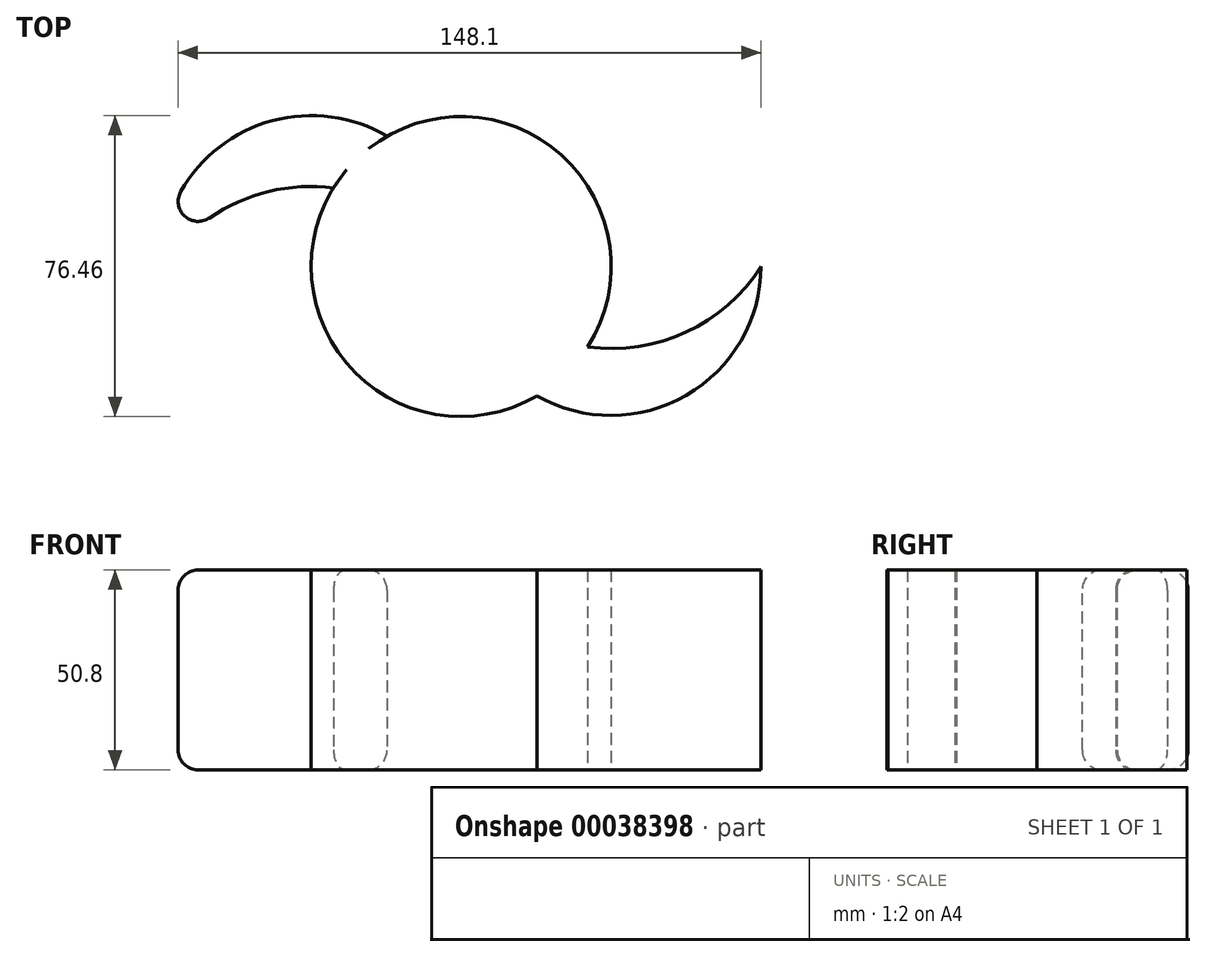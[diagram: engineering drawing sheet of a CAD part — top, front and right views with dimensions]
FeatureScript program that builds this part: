
annotation { "Feature Type Name" : "Feature", "Feature Type Description" : "" }
export const myFeature = defineFeature(function(context is Context, id is Id, definition is map)
    precondition{}
    {
        {
            var Q0;
            Q0=qCreatedBy(makeId("Top.planeOp"),FACE);
            var sketch = newSketch(context, id + "F0", { "sketchPlane" : qUnion([Q0])});
            skPoint(sketch, "E0", {"position": v(0, 0) * mm});
            skPoint(sketch, "E1", {"position": v(76.2, 0) * mm});
            skPoint(sketch, "E2", {"position": v(-76.2, 0) * mm});
            skArc(sketch, "E3", {"start": v(-18.83, 33.13) * mm, "mid": v(-57.15, 33.26) * mm, "end": v(-76.2, 0) * mm});
            skArc(sketch, "E4", {"start": v(19.27, -32.87) * mm, "mid": v(57.15, -32.74) * mm, "end": v(76.2, 0) * mm});
            skArc(sketch, "E5", {"start": v(-32.43, 20) * mm, "mid": v(-27.24, -26.64) * mm, "end": v(19.27, -32.87) * mm});
            skArc(sketch, "E6", {"start": v(-32.43, 20) * mm, "mid": v(-57.15, 16.2) * mm, "end": v(-76.2, 0) * mm});
            skArc(sketch, "E7", {"start": v(32.15, -20.45) * mm, "mid": v(57.15, -16.64) * mm, "end": v(76.2, 0) * mm});
            skArc(sketch, "E8.trimOffspring", {"start": v(32.15, -20.45) * mm, "mid": v(27.6, 26.26) * mm, "end": v(-18.83, 33.13) * mm});
            skSolve(sketch);
        }
        {
            var Q0;
            Q0 = qSketchRegion(id + "F0", true);
            extrude(context, id + "F1", {"entities" : qUnion([Q0]), "depth" : 50.8 * mm});
        }
        {
            var Q0;
            Q0=makeQuery(id+"F1.opExtrude","CAP_EDGE",EDGE,{"disambiguationData":[OSD([sQuery(id+"F0.wireOp",EDGE,"E3")])],"isStart":false});
            var Q1;
            Q1=makeQuery(id+"F1.opExtrude","CAP_EDGE",EDGE,{"disambiguationData":[OSD([sQuery(id+"F0.wireOp",EDGE,"E3")])],"isStart":true});
            var Q2;
            Q2=makeQuery(id+"F1.opExtrude","CAP_EDGE",EDGE,{"disambiguationData":[OSD([sQuery(id+"F0.wireOp",EDGE,"E6")])],"isStart":false});
            var Q3;
            Q3=makeQuery(id+"F1.opExtrude","CAP_EDGE",EDGE,{"disambiguationData":[OSD([sQuery(id+"F0.wireOp",EDGE,"E6")])],"isStart":true});
            fillet(context, id + "F2", {"entities" : qUnion([Q0, Q1, Q2, Q3]), "radius" : 5.08 * mm, "tangentPropagation" : true, "allowEdgeOverflow" : false});
        }
        {
            var Q0;
            Q0=makeQuery(id+"F1.opExtrude","SWEPT_EDGE",EDGE,{"disambiguationData":[OSD([sQuery(id+"F0.wireOp",EDGE,"E3"),sQuery(id+"F0.wireOp",EDGE,"E6")])]});
            var Q1;
            {var subQ0=sQuery(id+"F0.wireOp",EDGE,"E3");Q1=makeQuery(id+"F2.opFillet","BLEND_EDGE",EDGE,{"blendedFrom":[makeQuery(id+"F1.opExtrude","CAP_EDGE",EDGE,{"disambiguationData":[OSD([subQ0])],"isStart":true}),makeQuery(id+"F1.opExtrude","SWEPT_FACE",FACE,{"disambiguationData":[OSD([subQ0])]})],"blendedInto":[makeQuery(id+"F1.opExtrude","SWEPT_FACE",FACE,{"disambiguationData":[OSD([subQ0])]})]});}
            var Q2;
            {var subQ0=sQuery(id+"F0.wireOp",EDGE,"E6");Q2=makeQuery(id+"F2.opFillet","BLEND_EDGE",EDGE,{"blendedFrom":[makeQuery(id+"F1.opExtrude","CAP_EDGE",EDGE,{"disambiguationData":[OSD([subQ0])],"isStart":true}),makeQuery(id+"F1.opExtrude","CAP_FACE",FACE,{"disambiguationData":[OSD([sQuery(id+"F0.wireOp",EDGE,"E3"),sQuery(id+"F0.wireOp",EDGE,"E4"),sQuery(id+"F0.wireOp",EDGE,"E5"),subQ0,sQuery(id+"F0.wireOp",EDGE,"E7"),sQuery(id+"F0.wireOp",EDGE,"E8.trimOffspring")])],"isStart":true})],"blendedInto":[makeQuery(id+"F1.opExtrude","CAP_FACE",FACE,{"disambiguationData":[OSD([sQuery(id+"F0.wireOp",EDGE,"E3"),sQuery(id+"F0.wireOp",EDGE,"E4"),sQuery(id+"F0.wireOp",EDGE,"E5"),subQ0,sQuery(id+"F0.wireOp",EDGE,"E7"),sQuery(id+"F0.wireOp",EDGE,"E8.trimOffspring")])],"isStart":true})]});}
            var Q3;
            Q3=makeQuery(id+"F2.opFillet","BLEND_EDGE",EDGE,{"blendedFrom":[makeQuery(id+"F1.opExtrude","CAP_EDGE",EDGE,{"disambiguationData":[OSD([sQuery(id+"F0.wireOp",EDGE,"E3")])],"isStart":true}),makeQuery(id+"F1.opExtrude","CAP_EDGE",EDGE,{"disambiguationData":[OSD([sQuery(id+"F0.wireOp",EDGE,"E6")])],"isStart":true})],"blendedInto":[]});
            var Q4;
            {var subQ0=sQuery(id+"F0.wireOp",EDGE,"E6");Q4=makeQuery(id+"F2.opFillet","BLEND_EDGE",EDGE,{"blendedFrom":[makeQuery(id+"F1.opExtrude","CAP_EDGE",EDGE,{"disambiguationData":[OSD([subQ0])],"isStart":true}),makeQuery(id+"F1.opExtrude","SWEPT_FACE",FACE,{"disambiguationData":[OSD([subQ0])]})],"blendedInto":[makeQuery(id+"F1.opExtrude","SWEPT_FACE",FACE,{"disambiguationData":[OSD([subQ0])]})]});}
            fillet(context, id + "F3", {"entities" : qUnion([Q0, Q1, Q2, Q3, Q4]), "radius" : 5.08 * mm, "tangentPropagation" : true, "allowEdgeOverflow" : false});
        }
    });
